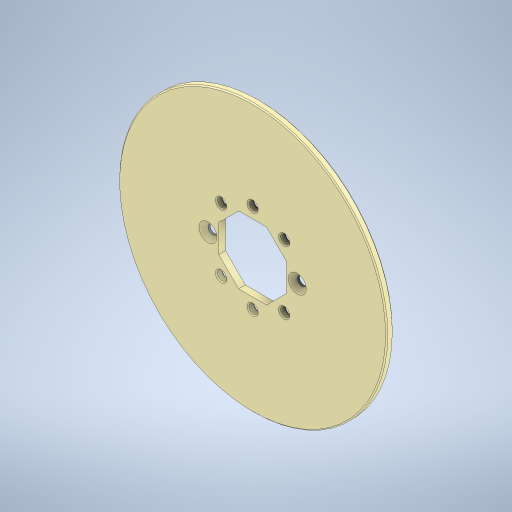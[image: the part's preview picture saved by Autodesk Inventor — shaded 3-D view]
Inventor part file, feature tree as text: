
AUTODESK INVENTOR PART (.ipt)
format: ipt  version: 2023.4 (Build 274418000, 418)  size: 344,064 bytes
history: native  units: mm
features: extrude x3, chamfer x2, sketch x2
ambient origin geometry x8: Origin, YZ Plane, XZ Plane, XY Plane, X Axis, Y Axis, Z Axis, Center Point
bodies: Solid1 (feature_tree)
feature tree (7):
  extrude  "Extrusion1"  Depth=3.0mm TaperAngle=0.0deg
  extrude  "Extrusion3"  Depth=80.0mm TaperAngle=360.0deg
  extrude  "Extrusion4"  TaperAngle=0.0deg  [1 undecoded]
  chamfer  "Chamfer1"  Distance=2.0mm Angle=45.0deg
  chamfer  "Chamfer2"  Distance=0.5mm Angle=45.0deg
  sketch  "Sketch3"  dims[d0=120.0mm d1=3.0mm d2=0.0mm]
  sketch  "Sketch4"  dims[d22=0.0mm d23=0.0mm d25=80.0mm d26=360.0deg d27=4.1mm d28=0.0mm d29=0.0mm d30=2.0mm d31=2.0mm d32=45.0deg d33=0.5mm d34=2.0mm d35=45.0deg]
note: 1 required parameter value undecoded (feature->parameter linkage not recoverable at this tier; creation-order binding heuristic only, values carry confidence <= 0.55)
